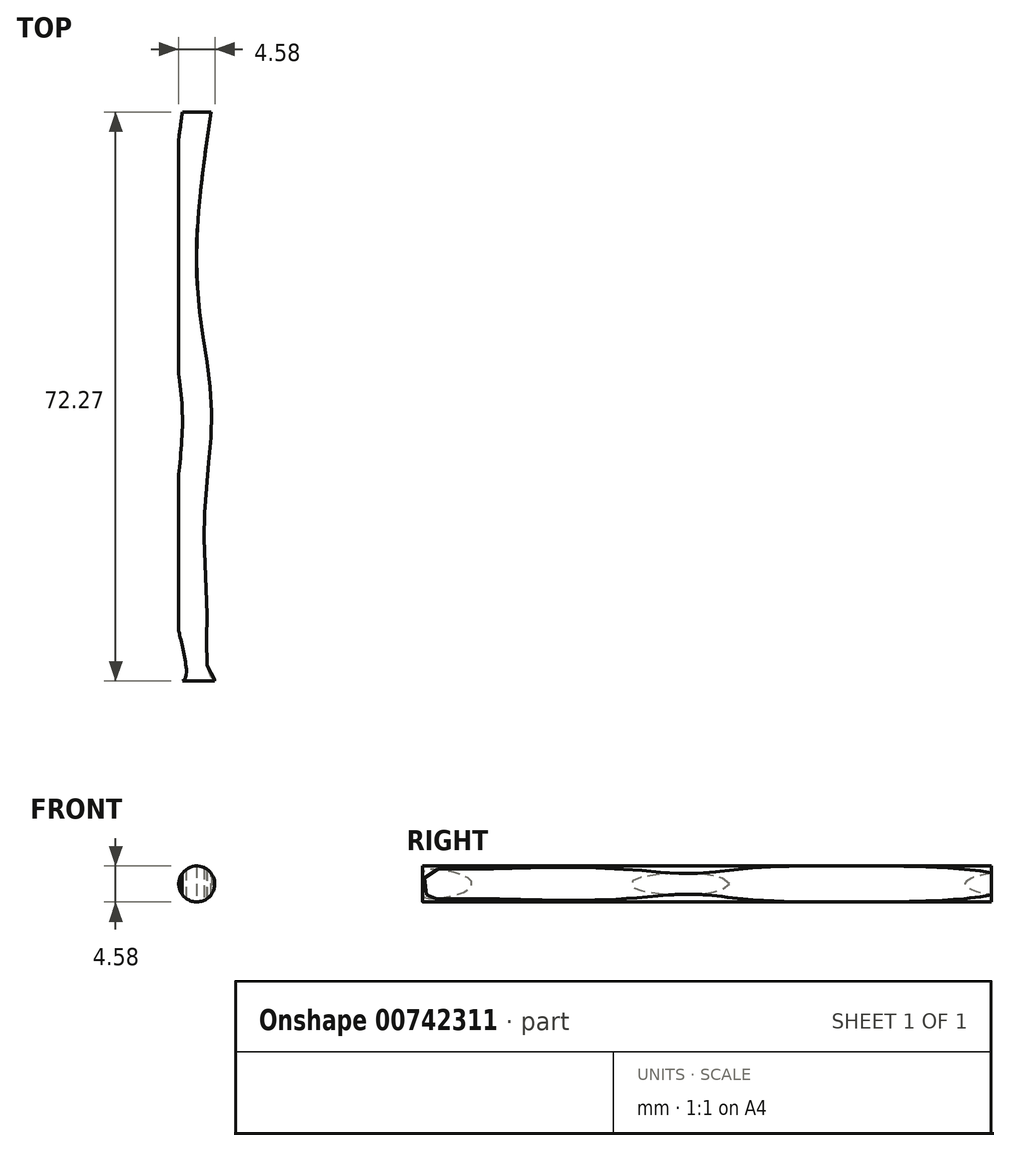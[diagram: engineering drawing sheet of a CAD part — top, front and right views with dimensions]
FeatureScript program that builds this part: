
annotation { "Feature Type Name" : "Feature", "Feature Type Description" : "" }
export const myFeature = defineFeature(function(context is Context, id is Id, definition is map)
    precondition{}
    {
        {
            var Q0;
            Q0=qCreatedBy(makeId("Front.planeOp"),FACE);
            var sketch = newSketch(context, id + "F0", { "sketchPlane" : qUnion([Q0])});
            skCircle(sketch, "E0", {"center": v(0, 0) * mm, "radius": 2.29 * mm});
            skCircle(sketch, "E1", {"center": v(0, 0) * mm, "radius": 2.54 * mm});
            skLineSegment(sketch, "E2.bottom", {"start": v(-4.49, 3.4) * mm, "end": v(4.49, 3.4) * mm});
            skLineSegment(sketch, "E2.top", {"start": v(-4.49, -3.4) * mm, "end": v(4.49, -3.4) * mm});
            skLineSegment(sketch, "E2.left", {"start": v(-4.49, 3.4) * mm, "end": v(-4.49, -3.4) * mm});
            skLineSegment(sketch, "E2.right", {"start": v(4.49, 3.4) * mm, "end": v(4.49, -3.4) * mm});
            skSolve(sketch);
        }
        {
            var Q0;
            Q0=qCreatedBy(makeId("Top.planeOp"),FACE);
            var sketch = newSketch(context, id + "F1", { "sketchPlane" : qUnion([Q0])});
            skLineSegment(sketch, "E3.0", {"start": v(-3.5, 0) * mm, "end": v(3.3, 0) * mm});
            skLineSegment(sketch, "E4.0", {"start": v(1.55, 0) * mm, "end": v(-2.94, 0.06) * mm});
            skLineSegment(sketch, "E5.0", {"start": v(2.52, 0.02) * mm, "end": v(-1.83, 0.04) * mm});
            skLineSegment(sketch, "E6.0", {"start": v(1.55, 0) * mm, "end": v(-1.75, 0) * mm});
            skLineSegment(sketch, "E7.0", {"start": v(1.8, 0) * mm, "end": v(-2, 0) * mm});
            skFitSpline(sketch, "E8", {"points": [v(-1.83, 0.04) * mm, v(-1.83, 0.06) * mm, v(-2.52, 7.47) * mm, v(-2.94, 20.11) * mm, v(-1.83, 33.54) * mm, v(-2.94, 43.33) * mm, v(-3.54, 56.15) * mm, v(-1.83, 72.3) * mm], "startDerivative": vector(-57.8, -0.16) * mm, "endDerivative": vector(6.35, 45.91) * mm});
            skFitSpline(sketch, "E9", {"points": [v(2.52, 0.02) * mm, v(1.8, 0.54) * mm, v(1.3, 7.46) * mm, v(0.94, 20.2) * mm, v(1.88, 33.63) * mm, v(0.82, 43.62) * mm, v(0, 56.36) * mm, v(1.8, 72.29) * mm], "startDerivative": vector(0.66, 8.52) * mm, "endDerivative": vector(6.35, 45.91) * mm});
            skLineSegment(sketch, "E10", {"start": v(-1.83, 72.3) * mm, "end": v(1.8, 72.29) * mm});
            skSolve(sketch);
        }
        {
            var Q0;
            Q0=makeQuery(id+"F0.imprint","IMPRINT",FACE,{"disambiguationData":[TD([[makeQuery(id+"F0.imprint","IMPRINT",EDGE,{"derivedFrom":sQuery(id+"F0.wireOp",EDGE,"E1")}),-1.0]])]});
            var Q1;
            Q1=makeQuery(id+"F0.imprint","IMPRINT",FACE,{"disambiguationData":[TD([[makeQuery(id+"F0.imprint","IMPRINT",EDGE,{"derivedFrom":sQuery(id+"F0.wireOp",EDGE,"E0")}),1.0]])]});
            var Q2;
            Q2=makeQuery(id+"F0.imprint","IMPRINT",FACE,{"disambiguationData":[TD([[makeQuery(id+"F0.imprint","IMPRINT",EDGE,{"derivedFrom":sQuery(id+"F0.wireOp",EDGE,"E0")}),-1.0]])]});
            extrude(context, id + "F2", {"entities" : qUnion([Q0, Q1, Q2]), "oppositeDirection" : true, "depth" : 75.95 * mm, "offsetDistance" : 25.4 * mm});
        }
        {
            var Q0;
            Q0 = qSketchRegion(id + "F1", true);
            extrude(context, id + "F3", {"entities" : qUnion([Q0]), "operationType" : NewBodyOperationType.INTERSECT, "endBound" : BoundingType.SYMMETRIC, "oppositeDirection" : true, "depth" : 80.77 * mm, "offsetDistance" : 25.4 * mm});
        }
        {
            var Q0;
            Q0=makeQuery(id+"F0.imprint","IMPRINT",FACE,{"disambiguationData":[TD([[makeQuery(id+"F0.imprint","IMPRINT",EDGE,{"derivedFrom":sQuery(id+"F0.wireOp",EDGE,"E0")}),1.0]])]});
            extrude(context, id + "F4", {"entities" : qUnion([Q0]), "operationType" : NewBodyOperationType.INTERSECT, "oppositeDirection" : true, "depth" : 75.64 * mm, "offsetDistance" : 25.4 * mm});
        }
    });
